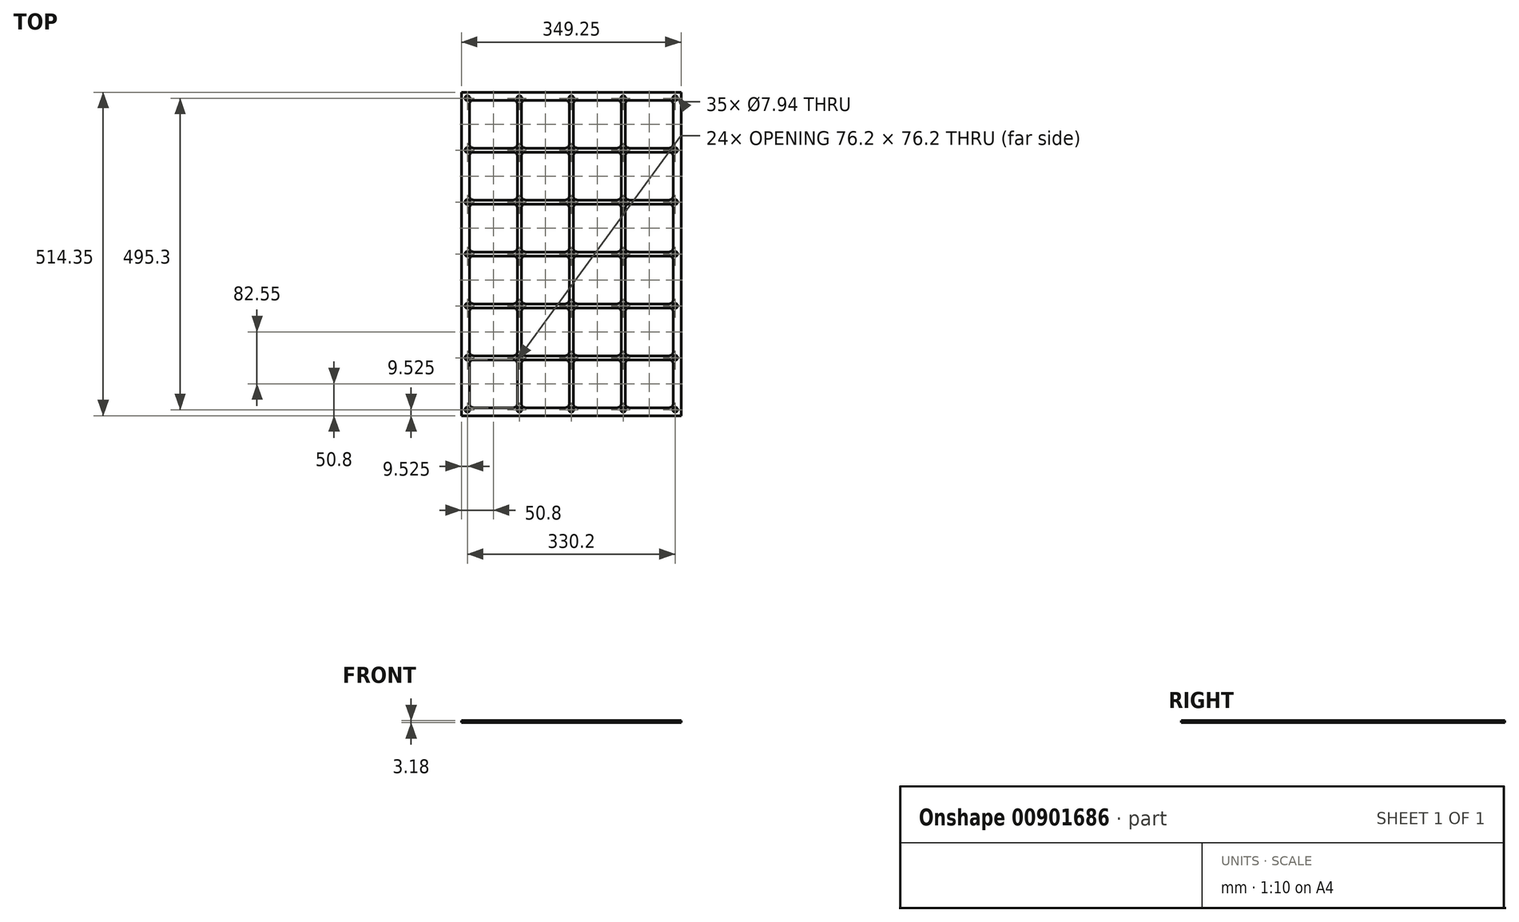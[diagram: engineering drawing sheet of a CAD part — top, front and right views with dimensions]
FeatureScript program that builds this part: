
annotation { "Feature Type Name" : "Feature", "Feature Type Description" : "" }
export const myFeature = defineFeature(function(context is Context, id is Id, definition is map)
    precondition{}
    {
        {
            var Q0;
            Q0=qCreatedBy(makeId("Top.planeOp"),FACE);
            var sketch = newSketch(context, id + "F0", { "sketchPlane" : qUnion([Q0])});
            skLineSegment(sketch, "E0.bottom", {"start": v(0, 0) * mm, "end": v(349.25, 0) * mm});
            skLineSegment(sketch, "E0.top", {"start": v(0, 514.35) * mm, "end": v(349.25, 514.35) * mm});
            skLineSegment(sketch, "E0.left", {"start": v(0, 0) * mm, "end": v(0, 514.35) * mm});
            skLineSegment(sketch, "E0.right", {"start": v(349.25, 0) * mm, "end": v(349.25, 514.35) * mm});
            skLineSegment(sketch, "E1.bottom", {"start": v(19.05, 12.7) * mm, "end": v(82.55, 12.7) * mm});
            skLineSegment(sketch, "E1.top", {"start": v(19.05, 88.9) * mm, "end": v(82.55, 88.9) * mm});
            skLineSegment(sketch, "E1.left", {"start": v(12.7, 19.05) * mm, "end": v(12.7, 82.55) * mm});
            skLineSegment(sketch, "E1.right", {"start": v(88.9, 19.05) * mm, "end": v(88.9, 82.55) * mm});
            skArc(sketch, "E2.filletArc", {"start": v(19.05, 88.9) * mm, "mid": v(14.56, 87.04) * mm, "end": v(12.7, 82.55) * mm});
            skArc(sketch, "E3.filletArc", {"start": v(88.9, 82.55) * mm, "mid": v(87.04, 87.04) * mm, "end": v(82.55, 88.9) * mm});
            skArc(sketch, "E4.filletArc", {"start": v(82.55, 12.7) * mm, "mid": v(87.04, 14.56) * mm, "end": v(88.9, 19.05) * mm});
            skArc(sketch, "E5.filletArc", {"start": v(12.7, 19.05) * mm, "mid": v(14.56, 14.56) * mm, "end": v(19.05, 12.7) * mm});
            skLineSegment(sketch, "E6.0.1.0", {"start": v(19.05, 171.45) * mm, "end": v(82.55, 171.45) * mm});
            skLineSegment(sketch, "E6.0.1.1", {"start": v(88.9, 101.6) * mm, "end": v(88.9, 165.1) * mm});
            skArc(sketch, "E6.0.1.2", {"start": v(88.9, 165.1) * mm, "mid": v(87.04, 169.6) * mm, "end": v(82.55, 171.45) * mm});
            skArc(sketch, "E6.0.1.3", {"start": v(82.55, 95.25) * mm, "mid": v(87.04, 97.1) * mm, "end": v(88.9, 101.6) * mm});
            skLineSegment(sketch, "E6.0.1.4", {"start": v(19.05, 95.25) * mm, "end": v(82.55, 95.25) * mm});
            skArc(sketch, "E6.0.1.5", {"start": v(12.7, 101.6) * mm, "mid": v(14.56, 97.1) * mm, "end": v(19.05, 95.25) * mm});
            skLineSegment(sketch, "E6.0.1.6", {"start": v(12.7, 101.6) * mm, "end": v(12.7, 165.1) * mm});
            skArc(sketch, "E6.0.1.7", {"start": v(19.05, 171.45) * mm, "mid": v(14.56, 169.6) * mm, "end": v(12.7, 165.1) * mm});
            skLineSegment(sketch, "E6.0.2.0", {"start": v(19.05, 254) * mm, "end": v(82.55, 254) * mm});
            skLineSegment(sketch, "E6.0.2.1", {"start": v(88.9, 184.15) * mm, "end": v(88.9, 247.65) * mm});
            skArc(sketch, "E6.0.2.2", {"start": v(88.9, 247.65) * mm, "mid": v(87.04, 252.14) * mm, "end": v(82.55, 254) * mm});
            skArc(sketch, "E6.0.2.3", {"start": v(82.55, 177.8) * mm, "mid": v(87.04, 179.66) * mm, "end": v(88.9, 184.15) * mm});
            skLineSegment(sketch, "E6.0.2.4", {"start": v(19.05, 177.8) * mm, "end": v(82.55, 177.8) * mm});
            skArc(sketch, "E6.0.2.5", {"start": v(12.7, 184.15) * mm, "mid": v(14.56, 179.66) * mm, "end": v(19.05, 177.8) * mm});
            skLineSegment(sketch, "E6.0.2.6", {"start": v(12.7, 184.15) * mm, "end": v(12.7, 247.65) * mm});
            skArc(sketch, "E6.0.2.7", {"start": v(19.05, 254) * mm, "mid": v(14.56, 252.14) * mm, "end": v(12.7, 247.65) * mm});
            skLineSegment(sketch, "E6.0.3.0", {"start": v(19.05, 336.55) * mm, "end": v(82.55, 336.55) * mm});
            skLineSegment(sketch, "E6.0.3.1", {"start": v(88.9, 266.7) * mm, "end": v(88.9, 330.2) * mm});
            skArc(sketch, "E6.0.3.2", {"start": v(88.9, 330.2) * mm, "mid": v(87.04, 334.7) * mm, "end": v(82.55, 336.55) * mm});
            skArc(sketch, "E6.0.3.3", {"start": v(82.55, 260.35) * mm, "mid": v(87.04, 262.2) * mm, "end": v(88.9, 266.7) * mm});
            skLineSegment(sketch, "E6.0.3.4", {"start": v(19.05, 260.35) * mm, "end": v(82.55, 260.35) * mm});
            skArc(sketch, "E6.0.3.5", {"start": v(12.7, 266.7) * mm, "mid": v(14.56, 262.2) * mm, "end": v(19.05, 260.35) * mm});
            skLineSegment(sketch, "E6.0.3.6", {"start": v(12.7, 266.7) * mm, "end": v(12.7, 330.2) * mm});
            skArc(sketch, "E6.0.3.7", {"start": v(19.05, 336.55) * mm, "mid": v(14.56, 334.7) * mm, "end": v(12.7, 330.2) * mm});
            skLineSegment(sketch, "E6.0.4.0", {"start": v(19.05, 419.1) * mm, "end": v(82.55, 419.1) * mm});
            skLineSegment(sketch, "E6.0.4.1", {"start": v(88.9, 349.25) * mm, "end": v(88.9, 412.75) * mm});
            skArc(sketch, "E6.0.4.2", {"start": v(88.9, 412.75) * mm, "mid": v(87.04, 417.24) * mm, "end": v(82.55, 419.1) * mm});
            skArc(sketch, "E6.0.4.3", {"start": v(82.55, 342.9) * mm, "mid": v(87.04, 344.76) * mm, "end": v(88.9, 349.25) * mm});
            skLineSegment(sketch, "E6.0.4.4", {"start": v(19.05, 342.9) * mm, "end": v(82.55, 342.9) * mm});
            skArc(sketch, "E6.0.4.5", {"start": v(12.7, 349.25) * mm, "mid": v(14.56, 344.76) * mm, "end": v(19.05, 342.9) * mm});
            skLineSegment(sketch, "E6.0.4.6", {"start": v(12.7, 349.25) * mm, "end": v(12.7, 412.75) * mm});
            skArc(sketch, "E6.0.4.7", {"start": v(19.05, 419.1) * mm, "mid": v(14.56, 417.24) * mm, "end": v(12.7, 412.75) * mm});
            skLineSegment(sketch, "E6.0.5.0", {"start": v(19.05, 501.65) * mm, "end": v(82.55, 501.65) * mm});
            skLineSegment(sketch, "E6.0.5.1", {"start": v(88.9, 431.8) * mm, "end": v(88.9, 495.3) * mm});
            skArc(sketch, "E6.0.5.2", {"start": v(88.9, 495.3) * mm, "mid": v(87.04, 499.8) * mm, "end": v(82.55, 501.65) * mm});
            skArc(sketch, "E6.0.5.3", {"start": v(82.55, 425.45) * mm, "mid": v(87.04, 427.3) * mm, "end": v(88.9, 431.8) * mm});
            skLineSegment(sketch, "E6.0.5.4", {"start": v(19.05, 425.45) * mm, "end": v(82.55, 425.45) * mm});
            skArc(sketch, "E6.0.5.5", {"start": v(12.7, 431.8) * mm, "mid": v(14.56, 427.3) * mm, "end": v(19.05, 425.45) * mm});
            skLineSegment(sketch, "E6.0.5.6", {"start": v(12.7, 431.8) * mm, "end": v(12.7, 495.3) * mm});
            skArc(sketch, "E6.0.5.7", {"start": v(19.05, 501.65) * mm, "mid": v(14.56, 499.8) * mm, "end": v(12.7, 495.3) * mm});
            skLineSegment(sketch, "E6.1.0.0", {"start": v(101.6, 88.9) * mm, "end": v(165.1, 88.9) * mm});
            skLineSegment(sketch, "E6.1.0.1", {"start": v(171.45, 19.05) * mm, "end": v(171.45, 82.55) * mm});
            skArc(sketch, "E6.1.0.2", {"start": v(171.45, 82.55) * mm, "mid": v(169.6, 87.04) * mm, "end": v(165.1, 88.9) * mm});
            skArc(sketch, "E6.1.0.3", {"start": v(165.1, 12.7) * mm, "mid": v(169.6, 14.56) * mm, "end": v(171.45, 19.05) * mm});
            skLineSegment(sketch, "E6.1.0.4", {"start": v(101.6, 12.7) * mm, "end": v(165.1, 12.7) * mm});
            skArc(sketch, "E6.1.0.5", {"start": v(95.25, 19.05) * mm, "mid": v(97.1, 14.56) * mm, "end": v(101.6, 12.7) * mm});
            skLineSegment(sketch, "E6.1.0.6", {"start": v(95.25, 19.05) * mm, "end": v(95.25, 82.55) * mm});
            skArc(sketch, "E6.1.0.7", {"start": v(101.6, 88.9) * mm, "mid": v(97.1, 87.04) * mm, "end": v(95.25, 82.55) * mm});
            skLineSegment(sketch, "E6.1.1.0", {"start": v(101.6, 171.45) * mm, "end": v(165.1, 171.45) * mm});
            skLineSegment(sketch, "E6.1.1.1", {"start": v(171.45, 101.6) * mm, "end": v(171.45, 165.1) * mm});
            skArc(sketch, "E6.1.1.2", {"start": v(171.45, 165.1) * mm, "mid": v(169.6, 169.6) * mm, "end": v(165.1, 171.45) * mm});
            skArc(sketch, "E6.1.1.3", {"start": v(165.1, 95.25) * mm, "mid": v(169.6, 97.1) * mm, "end": v(171.45, 101.6) * mm});
            skLineSegment(sketch, "E6.1.1.4", {"start": v(101.6, 95.25) * mm, "end": v(165.1, 95.25) * mm});
            skArc(sketch, "E6.1.1.5", {"start": v(95.25, 101.6) * mm, "mid": v(97.1, 97.1) * mm, "end": v(101.6, 95.25) * mm});
            skLineSegment(sketch, "E6.1.1.6", {"start": v(95.25, 101.6) * mm, "end": v(95.25, 165.1) * mm});
            skArc(sketch, "E6.1.1.7", {"start": v(101.6, 171.45) * mm, "mid": v(97.1, 169.6) * mm, "end": v(95.25, 165.1) * mm});
            skLineSegment(sketch, "E6.1.2.0", {"start": v(101.6, 254) * mm, "end": v(165.1, 254) * mm});
            skLineSegment(sketch, "E6.1.2.1", {"start": v(171.45, 184.15) * mm, "end": v(171.45, 247.65) * mm});
            skArc(sketch, "E6.1.2.2", {"start": v(171.45, 247.65) * mm, "mid": v(169.6, 252.14) * mm, "end": v(165.1, 254) * mm});
            skArc(sketch, "E6.1.2.3", {"start": v(165.1, 177.8) * mm, "mid": v(169.6, 179.66) * mm, "end": v(171.45, 184.15) * mm});
            skLineSegment(sketch, "E6.1.2.4", {"start": v(101.6, 177.8) * mm, "end": v(165.1, 177.8) * mm});
            skArc(sketch, "E6.1.2.5", {"start": v(95.25, 184.15) * mm, "mid": v(97.1, 179.66) * mm, "end": v(101.6, 177.8) * mm});
            skLineSegment(sketch, "E6.1.2.6", {"start": v(95.25, 184.15) * mm, "end": v(95.25, 247.65) * mm});
            skArc(sketch, "E6.1.2.7", {"start": v(101.6, 254) * mm, "mid": v(97.1, 252.14) * mm, "end": v(95.25, 247.65) * mm});
            skLineSegment(sketch, "E6.1.3.0", {"start": v(101.6, 336.55) * mm, "end": v(165.1, 336.55) * mm});
            skLineSegment(sketch, "E6.1.3.1", {"start": v(171.45, 266.7) * mm, "end": v(171.45, 330.2) * mm});
            skArc(sketch, "E6.1.3.2", {"start": v(171.45, 330.2) * mm, "mid": v(169.6, 334.7) * mm, "end": v(165.1, 336.55) * mm});
            skArc(sketch, "E6.1.3.3", {"start": v(165.1, 260.35) * mm, "mid": v(169.6, 262.2) * mm, "end": v(171.45, 266.7) * mm});
            skLineSegment(sketch, "E6.1.3.4", {"start": v(101.6, 260.35) * mm, "end": v(165.1, 260.35) * mm});
            skArc(sketch, "E6.1.3.5", {"start": v(95.25, 266.7) * mm, "mid": v(97.1, 262.2) * mm, "end": v(101.6, 260.35) * mm});
            skLineSegment(sketch, "E6.1.3.6", {"start": v(95.25, 266.7) * mm, "end": v(95.25, 330.2) * mm});
            skArc(sketch, "E6.1.3.7", {"start": v(101.6, 336.55) * mm, "mid": v(97.1, 334.7) * mm, "end": v(95.25, 330.2) * mm});
            skLineSegment(sketch, "E6.1.4.0", {"start": v(101.6, 419.1) * mm, "end": v(165.1, 419.1) * mm});
            skLineSegment(sketch, "E6.1.4.1", {"start": v(171.45, 349.25) * mm, "end": v(171.45, 412.75) * mm});
            skArc(sketch, "E6.1.4.2", {"start": v(171.45, 412.75) * mm, "mid": v(169.6, 417.24) * mm, "end": v(165.1, 419.1) * mm});
            skArc(sketch, "E6.1.4.3", {"start": v(165.1, 342.9) * mm, "mid": v(169.6, 344.76) * mm, "end": v(171.45, 349.25) * mm});
            skLineSegment(sketch, "E6.1.4.4", {"start": v(101.6, 342.9) * mm, "end": v(165.1, 342.9) * mm});
            skArc(sketch, "E6.1.4.5", {"start": v(95.25, 349.25) * mm, "mid": v(97.1, 344.76) * mm, "end": v(101.6, 342.9) * mm});
            skLineSegment(sketch, "E6.1.4.6", {"start": v(95.25, 349.25) * mm, "end": v(95.25, 412.75) * mm});
            skArc(sketch, "E6.1.4.7", {"start": v(101.6, 419.1) * mm, "mid": v(97.1, 417.24) * mm, "end": v(95.25, 412.75) * mm});
            skLineSegment(sketch, "E6.1.5.0", {"start": v(101.6, 501.65) * mm, "end": v(165.1, 501.65) * mm});
            skLineSegment(sketch, "E6.1.5.1", {"start": v(171.45, 431.8) * mm, "end": v(171.45, 495.3) * mm});
            skArc(sketch, "E6.1.5.2", {"start": v(171.45, 495.3) * mm, "mid": v(169.6, 499.8) * mm, "end": v(165.1, 501.65) * mm});
            skArc(sketch, "E6.1.5.3", {"start": v(165.1, 425.45) * mm, "mid": v(169.6, 427.3) * mm, "end": v(171.45, 431.8) * mm});
            skLineSegment(sketch, "E6.1.5.4", {"start": v(101.6, 425.45) * mm, "end": v(165.1, 425.45) * mm});
            skArc(sketch, "E6.1.5.5", {"start": v(95.25, 431.8) * mm, "mid": v(97.1, 427.3) * mm, "end": v(101.6, 425.45) * mm});
            skLineSegment(sketch, "E6.1.5.6", {"start": v(95.25, 431.8) * mm, "end": v(95.25, 495.3) * mm});
            skArc(sketch, "E6.1.5.7", {"start": v(101.6, 501.65) * mm, "mid": v(97.1, 499.8) * mm, "end": v(95.25, 495.3) * mm});
            skLineSegment(sketch, "E6.2.0.0", {"start": v(184.15, 88.9) * mm, "end": v(247.65, 88.9) * mm});
            skLineSegment(sketch, "E6.2.0.1", {"start": v(254, 19.05) * mm, "end": v(254, 82.55) * mm});
            skArc(sketch, "E6.2.0.2", {"start": v(254, 82.55) * mm, "mid": v(252.14, 87.04) * mm, "end": v(247.65, 88.9) * mm});
            skArc(sketch, "E6.2.0.3", {"start": v(247.65, 12.7) * mm, "mid": v(252.14, 14.56) * mm, "end": v(254, 19.05) * mm});
            skLineSegment(sketch, "E6.2.0.4", {"start": v(184.15, 12.7) * mm, "end": v(247.65, 12.7) * mm});
            skArc(sketch, "E6.2.0.5", {"start": v(177.8, 19.05) * mm, "mid": v(179.66, 14.56) * mm, "end": v(184.15, 12.7) * mm});
            skLineSegment(sketch, "E6.2.0.6", {"start": v(177.8, 19.05) * mm, "end": v(177.8, 82.55) * mm});
            skArc(sketch, "E6.2.0.7", {"start": v(184.15, 88.9) * mm, "mid": v(179.66, 87.04) * mm, "end": v(177.8, 82.55) * mm});
            skLineSegment(sketch, "E6.2.1.0", {"start": v(184.15, 171.45) * mm, "end": v(247.65, 171.45) * mm});
            skLineSegment(sketch, "E6.2.1.1", {"start": v(254, 101.6) * mm, "end": v(254, 165.1) * mm});
            skArc(sketch, "E6.2.1.2", {"start": v(254, 165.1) * mm, "mid": v(252.14, 169.6) * mm, "end": v(247.65, 171.45) * mm});
            skArc(sketch, "E6.2.1.3", {"start": v(247.65, 95.25) * mm, "mid": v(252.14, 97.1) * mm, "end": v(254, 101.6) * mm});
            skLineSegment(sketch, "E6.2.1.4", {"start": v(184.15, 95.25) * mm, "end": v(247.65, 95.25) * mm});
            skArc(sketch, "E6.2.1.5", {"start": v(177.8, 101.6) * mm, "mid": v(179.66, 97.1) * mm, "end": v(184.15, 95.25) * mm});
            skLineSegment(sketch, "E6.2.1.6", {"start": v(177.8, 101.6) * mm, "end": v(177.8, 165.1) * mm});
            skArc(sketch, "E6.2.1.7", {"start": v(184.15, 171.45) * mm, "mid": v(179.66, 169.6) * mm, "end": v(177.8, 165.1) * mm});
            skLineSegment(sketch, "E6.2.2.0", {"start": v(184.15, 254) * mm, "end": v(247.65, 254) * mm});
            skLineSegment(sketch, "E6.2.2.1", {"start": v(254, 184.15) * mm, "end": v(254, 247.65) * mm});
            skArc(sketch, "E6.2.2.2", {"start": v(254, 247.65) * mm, "mid": v(252.14, 252.14) * mm, "end": v(247.65, 254) * mm});
            skArc(sketch, "E6.2.2.3", {"start": v(247.65, 177.8) * mm, "mid": v(252.14, 179.66) * mm, "end": v(254, 184.15) * mm});
            skLineSegment(sketch, "E6.2.2.4", {"start": v(184.15, 177.8) * mm, "end": v(247.65, 177.8) * mm});
            skArc(sketch, "E6.2.2.5", {"start": v(177.8, 184.15) * mm, "mid": v(179.66, 179.66) * mm, "end": v(184.15, 177.8) * mm});
            skLineSegment(sketch, "E6.2.2.6", {"start": v(177.8, 184.15) * mm, "end": v(177.8, 247.65) * mm});
            skArc(sketch, "E6.2.2.7", {"start": v(184.15, 254) * mm, "mid": v(179.66, 252.14) * mm, "end": v(177.8, 247.65) * mm});
            skLineSegment(sketch, "E6.2.3.0", {"start": v(184.15, 336.55) * mm, "end": v(247.65, 336.55) * mm});
            skLineSegment(sketch, "E6.2.3.1", {"start": v(254, 266.7) * mm, "end": v(254, 330.2) * mm});
            skArc(sketch, "E6.2.3.2", {"start": v(254, 330.2) * mm, "mid": v(252.14, 334.7) * mm, "end": v(247.65, 336.55) * mm});
            skArc(sketch, "E6.2.3.3", {"start": v(247.65, 260.35) * mm, "mid": v(252.14, 262.2) * mm, "end": v(254, 266.7) * mm});
            skLineSegment(sketch, "E6.2.3.4", {"start": v(184.15, 260.35) * mm, "end": v(247.65, 260.35) * mm});
            skArc(sketch, "E6.2.3.5", {"start": v(177.8, 266.7) * mm, "mid": v(179.66, 262.2) * mm, "end": v(184.15, 260.35) * mm});
            skLineSegment(sketch, "E6.2.3.6", {"start": v(177.8, 266.7) * mm, "end": v(177.8, 330.2) * mm});
            skArc(sketch, "E6.2.3.7", {"start": v(184.15, 336.55) * mm, "mid": v(179.66, 334.7) * mm, "end": v(177.8, 330.2) * mm});
            skLineSegment(sketch, "E6.2.4.0", {"start": v(184.15, 419.1) * mm, "end": v(247.65, 419.1) * mm});
            skLineSegment(sketch, "E6.2.4.1", {"start": v(254, 349.25) * mm, "end": v(254, 412.75) * mm});
            skArc(sketch, "E6.2.4.2", {"start": v(254, 412.75) * mm, "mid": v(252.14, 417.24) * mm, "end": v(247.65, 419.1) * mm});
            skArc(sketch, "E6.2.4.3", {"start": v(247.65, 342.9) * mm, "mid": v(252.14, 344.76) * mm, "end": v(254, 349.25) * mm});
            skLineSegment(sketch, "E6.2.4.4", {"start": v(184.15, 342.9) * mm, "end": v(247.65, 342.9) * mm});
            skArc(sketch, "E6.2.4.5", {"start": v(177.8, 349.25) * mm, "mid": v(179.66, 344.76) * mm, "end": v(184.15, 342.9) * mm});
            skLineSegment(sketch, "E6.2.4.6", {"start": v(177.8, 349.25) * mm, "end": v(177.8, 412.75) * mm});
            skArc(sketch, "E6.2.4.7", {"start": v(184.15, 419.1) * mm, "mid": v(179.66, 417.24) * mm, "end": v(177.8, 412.75) * mm});
            skLineSegment(sketch, "E6.2.5.0", {"start": v(184.15, 501.65) * mm, "end": v(247.65, 501.65) * mm});
            skLineSegment(sketch, "E6.2.5.1", {"start": v(254, 431.8) * mm, "end": v(254, 495.3) * mm});
            skArc(sketch, "E6.2.5.2", {"start": v(254, 495.3) * mm, "mid": v(252.14, 499.8) * mm, "end": v(247.65, 501.65) * mm});
            skArc(sketch, "E6.2.5.3", {"start": v(247.65, 425.45) * mm, "mid": v(252.14, 427.3) * mm, "end": v(254, 431.8) * mm});
            skLineSegment(sketch, "E6.2.5.4", {"start": v(184.15, 425.45) * mm, "end": v(247.65, 425.45) * mm});
            skArc(sketch, "E6.2.5.5", {"start": v(177.8, 431.8) * mm, "mid": v(179.66, 427.3) * mm, "end": v(184.15, 425.45) * mm});
            skLineSegment(sketch, "E6.2.5.6", {"start": v(177.8, 431.8) * mm, "end": v(177.8, 495.3) * mm});
            skArc(sketch, "E6.2.5.7", {"start": v(184.15, 501.65) * mm, "mid": v(179.66, 499.8) * mm, "end": v(177.8, 495.3) * mm});
            skLineSegment(sketch, "E6.3.0.0", {"start": v(266.7, 88.9) * mm, "end": v(330.2, 88.9) * mm});
            skLineSegment(sketch, "E6.3.0.1", {"start": v(336.55, 19.05) * mm, "end": v(336.55, 82.55) * mm});
            skArc(sketch, "E6.3.0.2", {"start": v(336.55, 82.55) * mm, "mid": v(334.7, 87.04) * mm, "end": v(330.2, 88.9) * mm});
            skArc(sketch, "E6.3.0.3", {"start": v(330.2, 12.7) * mm, "mid": v(334.7, 14.56) * mm, "end": v(336.55, 19.05) * mm});
            skLineSegment(sketch, "E6.3.0.4", {"start": v(266.7, 12.7) * mm, "end": v(330.2, 12.7) * mm});
            skArc(sketch, "E6.3.0.5", {"start": v(260.35, 19.05) * mm, "mid": v(262.2, 14.56) * mm, "end": v(266.7, 12.7) * mm});
            skLineSegment(sketch, "E6.3.0.6", {"start": v(260.35, 19.05) * mm, "end": v(260.35, 82.55) * mm});
            skArc(sketch, "E6.3.0.7", {"start": v(266.7, 88.9) * mm, "mid": v(262.2, 87.04) * mm, "end": v(260.35, 82.55) * mm});
            skLineSegment(sketch, "E6.3.1.0", {"start": v(266.7, 171.45) * mm, "end": v(330.2, 171.45) * mm});
            skLineSegment(sketch, "E6.3.1.1", {"start": v(336.55, 101.6) * mm, "end": v(336.55, 165.1) * mm});
            skArc(sketch, "E6.3.1.2", {"start": v(336.55, 165.1) * mm, "mid": v(334.7, 169.6) * mm, "end": v(330.2, 171.45) * mm});
            skArc(sketch, "E6.3.1.3", {"start": v(330.2, 95.25) * mm, "mid": v(334.7, 97.1) * mm, "end": v(336.55, 101.6) * mm});
            skLineSegment(sketch, "E6.3.1.4", {"start": v(266.7, 95.25) * mm, "end": v(330.2, 95.25) * mm});
            skArc(sketch, "E6.3.1.5", {"start": v(260.35, 101.6) * mm, "mid": v(262.2, 97.1) * mm, "end": v(266.7, 95.25) * mm});
            skLineSegment(sketch, "E6.3.1.6", {"start": v(260.35, 101.6) * mm, "end": v(260.35, 165.1) * mm});
            skArc(sketch, "E6.3.1.7", {"start": v(266.7, 171.45) * mm, "mid": v(262.2, 169.6) * mm, "end": v(260.35, 165.1) * mm});
            skLineSegment(sketch, "E6.3.2.0", {"start": v(266.7, 254) * mm, "end": v(330.2, 254) * mm});
            skLineSegment(sketch, "E6.3.2.1", {"start": v(336.55, 184.15) * mm, "end": v(336.55, 247.65) * mm});
            skArc(sketch, "E6.3.2.2", {"start": v(336.55, 247.65) * mm, "mid": v(334.7, 252.14) * mm, "end": v(330.2, 254) * mm});
            skArc(sketch, "E6.3.2.3", {"start": v(330.2, 177.8) * mm, "mid": v(334.7, 179.66) * mm, "end": v(336.55, 184.15) * mm});
            skLineSegment(sketch, "E6.3.2.4", {"start": v(266.7, 177.8) * mm, "end": v(330.2, 177.8) * mm});
            skArc(sketch, "E6.3.2.5", {"start": v(260.35, 184.15) * mm, "mid": v(262.2, 179.66) * mm, "end": v(266.7, 177.8) * mm});
            skLineSegment(sketch, "E6.3.2.6", {"start": v(260.35, 184.15) * mm, "end": v(260.35, 247.65) * mm});
            skArc(sketch, "E6.3.2.7", {"start": v(266.7, 254) * mm, "mid": v(262.2, 252.14) * mm, "end": v(260.35, 247.65) * mm});
            skLineSegment(sketch, "E6.3.3.0", {"start": v(266.7, 336.55) * mm, "end": v(330.2, 336.55) * mm});
            skLineSegment(sketch, "E6.3.3.1", {"start": v(336.55, 266.7) * mm, "end": v(336.55, 330.2) * mm});
            skArc(sketch, "E6.3.3.2", {"start": v(336.55, 330.2) * mm, "mid": v(334.7, 334.7) * mm, "end": v(330.2, 336.55) * mm});
            skArc(sketch, "E6.3.3.3", {"start": v(330.2, 260.35) * mm, "mid": v(334.7, 262.2) * mm, "end": v(336.55, 266.7) * mm});
            skLineSegment(sketch, "E6.3.3.4", {"start": v(266.7, 260.35) * mm, "end": v(330.2, 260.35) * mm});
            skArc(sketch, "E6.3.3.5", {"start": v(260.35, 266.7) * mm, "mid": v(262.2, 262.2) * mm, "end": v(266.7, 260.35) * mm});
            skLineSegment(sketch, "E6.3.3.6", {"start": v(260.35, 266.7) * mm, "end": v(260.35, 330.2) * mm});
            skArc(sketch, "E6.3.3.7", {"start": v(266.7, 336.55) * mm, "mid": v(262.2, 334.7) * mm, "end": v(260.35, 330.2) * mm});
            skLineSegment(sketch, "E6.3.4.0", {"start": v(266.7, 419.1) * mm, "end": v(330.2, 419.1) * mm});
            skLineSegment(sketch, "E6.3.4.1", {"start": v(336.55, 349.25) * mm, "end": v(336.55, 412.75) * mm});
            skArc(sketch, "E6.3.4.2", {"start": v(336.55, 412.75) * mm, "mid": v(334.7, 417.24) * mm, "end": v(330.2, 419.1) * mm});
            skArc(sketch, "E6.3.4.3", {"start": v(330.2, 342.9) * mm, "mid": v(334.7, 344.76) * mm, "end": v(336.55, 349.25) * mm});
            skLineSegment(sketch, "E6.3.4.4", {"start": v(266.7, 342.9) * mm, "end": v(330.2, 342.9) * mm});
            skArc(sketch, "E6.3.4.5", {"start": v(260.35, 349.25) * mm, "mid": v(262.2, 344.76) * mm, "end": v(266.7, 342.9) * mm});
            skLineSegment(sketch, "E6.3.4.6", {"start": v(260.35, 349.25) * mm, "end": v(260.35, 412.75) * mm});
            skArc(sketch, "E6.3.4.7", {"start": v(266.7, 419.1) * mm, "mid": v(262.2, 417.24) * mm, "end": v(260.35, 412.75) * mm});
            skLineSegment(sketch, "E6.3.5.0", {"start": v(266.7, 501.65) * mm, "end": v(330.2, 501.65) * mm});
            skLineSegment(sketch, "E6.3.5.1", {"start": v(336.55, 431.8) * mm, "end": v(336.55, 495.3) * mm});
            skArc(sketch, "E6.3.5.2", {"start": v(336.55, 495.3) * mm, "mid": v(334.7, 499.8) * mm, "end": v(330.2, 501.65) * mm});
            skArc(sketch, "E6.3.5.3", {"start": v(330.2, 425.45) * mm, "mid": v(334.7, 427.3) * mm, "end": v(336.55, 431.8) * mm});
            skLineSegment(sketch, "E6.3.5.4", {"start": v(266.7, 425.45) * mm, "end": v(330.2, 425.45) * mm});
            skArc(sketch, "E6.3.5.5", {"start": v(260.35, 431.8) * mm, "mid": v(262.2, 427.3) * mm, "end": v(266.7, 425.45) * mm});
            skLineSegment(sketch, "E6.3.5.6", {"start": v(260.35, 431.8) * mm, "end": v(260.35, 495.3) * mm});
            skArc(sketch, "E6.3.5.7", {"start": v(266.7, 501.65) * mm, "mid": v(262.2, 499.8) * mm, "end": v(260.35, 495.3) * mm});
            skLineSegment(sketch, "E6.direction1", {"start": v(19.05, 12.7) * mm, "end": v(101.6, 12.7) * mm, "construction": true});
            skLineSegment(sketch, "E6.direction2", {"start": v(19.05, 12.7) * mm, "end": v(19.05, 95.25) * mm, "construction": true});
            skLineSegment(sketch, "E7", {"start": v(165.1, 101.6) * mm, "end": v(184.15, 82.55) * mm, "construction": true});
            skLineSegment(sketch, "E8", {"start": v(266.7, 101.6) * mm, "end": v(247.65, 82.55) * mm, "construction": true});
            skLineSegment(sketch, "E9", {"start": v(247.65, 184.15) * mm, "end": v(266.7, 165.1) * mm, "construction": true});
            skLineSegment(sketch, "E10", {"start": v(184.15, 184.15) * mm, "end": v(165.1, 165.1) * mm, "construction": true});
            skLineSegment(sketch, "E11", {"start": v(174.63, 174.63) * mm, "end": v(174.63, 92.08) * mm, "construction": true});
            skLineSegment(sketch, "E12", {"start": v(174.63, 92.08) * mm, "end": v(257.18, 92.08) * mm, "construction": true});
            skCircle(sketch, "E13", {"center": v(9.53, 9.53) * mm, "radius": 3.97 * mm});
            skCircle(sketch, "E14.0.1.0", {"center": v(9.53, 92.08) * mm, "radius": 3.97 * mm});
            skCircle(sketch, "E14.0.2.0", {"center": v(9.53, 174.63) * mm, "radius": 3.97 * mm});
            skCircle(sketch, "E14.0.3.0", {"center": v(9.53, 257.18) * mm, "radius": 3.97 * mm});
            skCircle(sketch, "E14.0.4.0", {"center": v(9.53, 339.73) * mm, "radius": 3.97 * mm});
            skCircle(sketch, "E14.0.5.0", {"center": v(9.53, 422.28) * mm, "radius": 3.97 * mm});
            skCircle(sketch, "E14.0.6.0", {"center": v(9.53, 504.83) * mm, "radius": 3.97 * mm});
            skCircle(sketch, "E14.1.0.0", {"center": v(92.08, 9.53) * mm, "radius": 3.97 * mm});
            skCircle(sketch, "E14.1.1.0", {"center": v(92.08, 92.08) * mm, "radius": 3.97 * mm});
            skCircle(sketch, "E14.1.2.0", {"center": v(92.08, 174.63) * mm, "radius": 3.97 * mm});
            skCircle(sketch, "E14.1.3.0", {"center": v(92.08, 257.18) * mm, "radius": 3.97 * mm});
            skCircle(sketch, "E14.1.4.0", {"center": v(92.08, 339.73) * mm, "radius": 3.97 * mm});
            skCircle(sketch, "E14.1.5.0", {"center": v(92.08, 422.28) * mm, "radius": 3.97 * mm});
            skCircle(sketch, "E14.1.6.0", {"center": v(92.08, 504.83) * mm, "radius": 3.97 * mm});
            skCircle(sketch, "E14.2.0.0", {"center": v(174.63, 9.53) * mm, "radius": 3.97 * mm});
            skCircle(sketch, "E14.2.1.0", {"center": v(174.63, 92.08) * mm, "radius": 3.97 * mm});
            skCircle(sketch, "E14.2.2.0", {"center": v(174.63, 174.63) * mm, "radius": 3.97 * mm});
            skCircle(sketch, "E14.2.3.0", {"center": v(174.63, 257.18) * mm, "radius": 3.97 * mm});
            skCircle(sketch, "E14.2.4.0", {"center": v(174.63, 339.73) * mm, "radius": 3.97 * mm});
            skCircle(sketch, "E14.2.5.0", {"center": v(174.63, 422.28) * mm, "radius": 3.97 * mm});
            skCircle(sketch, "E14.2.6.0", {"center": v(174.63, 504.83) * mm, "radius": 3.97 * mm});
            skCircle(sketch, "E14.3.0.0", {"center": v(257.18, 9.53) * mm, "radius": 3.97 * mm});
            skCircle(sketch, "E14.3.1.0", {"center": v(257.18, 92.08) * mm, "radius": 3.97 * mm});
            skCircle(sketch, "E14.3.2.0", {"center": v(257.18, 174.63) * mm, "radius": 3.97 * mm});
            skCircle(sketch, "E14.3.3.0", {"center": v(257.18, 257.18) * mm, "radius": 3.97 * mm});
            skCircle(sketch, "E14.3.4.0", {"center": v(257.18, 339.73) * mm, "radius": 3.97 * mm});
            skCircle(sketch, "E14.3.5.0", {"center": v(257.18, 422.28) * mm, "radius": 3.97 * mm});
            skCircle(sketch, "E14.3.6.0", {"center": v(257.18, 504.83) * mm, "radius": 3.97 * mm});
            skCircle(sketch, "E14.4.0.0", {"center": v(339.73, 9.53) * mm, "radius": 3.97 * mm});
            skCircle(sketch, "E14.4.1.0", {"center": v(339.73, 92.08) * mm, "radius": 3.97 * mm});
            skCircle(sketch, "E14.4.2.0", {"center": v(339.73, 174.63) * mm, "radius": 3.97 * mm});
            skCircle(sketch, "E14.4.3.0", {"center": v(339.73, 257.18) * mm, "radius": 3.97 * mm});
            skCircle(sketch, "E14.4.4.0", {"center": v(339.73, 339.73) * mm, "radius": 3.97 * mm});
            skCircle(sketch, "E14.4.5.0", {"center": v(339.73, 422.28) * mm, "radius": 3.97 * mm});
            skCircle(sketch, "E14.4.6.0", {"center": v(339.73, 504.83) * mm, "radius": 3.97 * mm});
            skLineSegment(sketch, "E14.direction1", {"start": v(9.53, 9.53) * mm, "end": v(92.08, 9.53) * mm, "construction": true});
            skLineSegment(sketch, "E14.direction2", {"start": v(9.53, 9.53) * mm, "end": v(9.53, 92.08) * mm, "construction": true});
            skSolve(sketch);
        }
        {
            var Q0;
            Q0=makeQuery(id+"F0.imprint","IMPRINT",FACE,{"disambiguationData":[TD([[makeQuery(id+"F0.imprint","IMPRINT",EDGE,{"derivedFrom":sQuery(id+"F0.wireOp",EDGE,"E0.bottom")}),1.0]])]});
            extrude(context, id + "F1", {"entities" : qUnion([Q0]), "depth" : 3.17 * mm, "offsetDistance" : 25.4 * mm});
        }
    });
